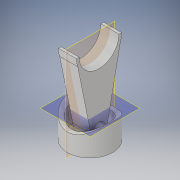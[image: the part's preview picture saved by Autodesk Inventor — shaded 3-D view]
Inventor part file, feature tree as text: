
AUTODESK INVENTOR PART (.ipt)
format: ipt  version: 2018 (Build 220112000, 112)  size: 163,840 bytes
history: native  units: in
note: dims shown in document units (in); Inventor stores cm internally (conversion verified against a paired STEP export)
features: sketch x5, extrude x5, plane x1
ambient origin geometry x8: Origin, YZ Plane, XZ Plane, XY Plane, X Axis, Y Axis, Z Axis, Center Point
bodies: Solid1 (feature_tree)
feature tree (11):
  sketch  "Sketch1"  dims[d0=0.5in d1=0.3in d2=0.0in]
  extrude  "Extrusion1"  Depth=0.3in TaperAngle=0.0deg
  extrude  "Extrusion2"  Depth=0.35in
  plane  "Work Plane1"
  extrude  "Extrusion3"  [1 undecoded]
  extrude  "Extrusion4"  Depth=0.25in TaperAngle=0.0deg
  extrude  "Extrusion5"  Depth=0.2in
  sketch  "Sketch2"  dims[d5=0.1in d6=0.35in]
  sketch  "Sketch3"  dims[d7=1.0in d8=0.0in d9=-0.3in]
  sketch  "Sketch4"  dims[d10=0.4in d11=0.25in d12=0.0in]
  sketch  "Sketch5"  dims[d13=0.1in d14=0.1in d15=0.45in d16=0.0in d17=0.14in d18=0.18in d21=0.44in d22=0.0in d23=0.8in d26=0.5in d27=0.2in d28=0.0in]
note: 1 required parameter value undecoded (feature->parameter linkage not recoverable at this tier; creation-order binding heuristic only, values carry confidence <= 0.55)
